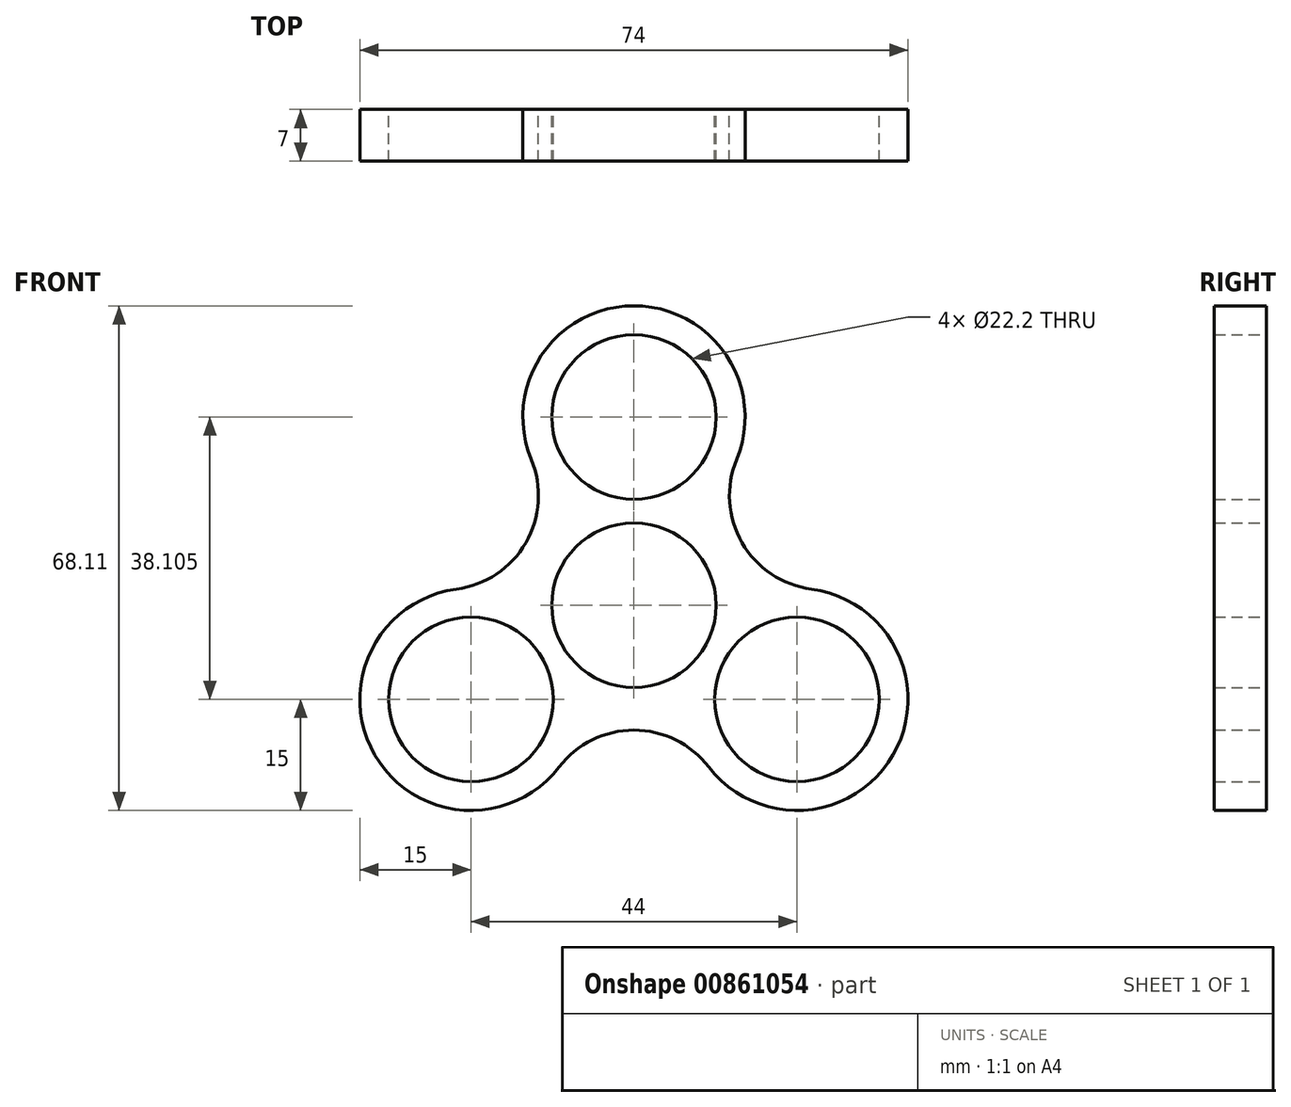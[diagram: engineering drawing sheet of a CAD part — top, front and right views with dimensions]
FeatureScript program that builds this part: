
annotation { "Feature Type Name" : "Feature", "Feature Type Description" : "" }
export const myFeature = defineFeature(function(context is Context, id is Id, definition is map)
    precondition{}
    {
        {
            var Q0;
            Q0=qCreatedBy(makeId("Front.planeOp"),FACE);
            var sketch = newSketch(context, id + "F0", { "sketchPlane" : qUnion([Q0])});
            skLineSegment(sketch, "E0", {"start": v(-22, 0) * mm, "end": v(22, 0) * mm});
            skLineSegment(sketch, "E1", {"start": v(22, 0) * mm, "end": v(0, 38.1) * mm});
            skLineSegment(sketch, "E2", {"start": v(0, 38.1) * mm, "end": v(-22, 0) * mm});
            skCircle(sketch, "E3", {"center": v(22, 0) * mm, "radius": 15 * mm});
            skCircle(sketch, "E4", {"center": v(0, 38.1) * mm, "radius": 15 * mm});
            skCircle(sketch, "E5", {"center": v(-22, 0) * mm, "radius": 15 * mm});
            skLineSegment(sketch, "E6", {"start": v(22, 0) * mm, "end": v(-25.63, 27.5) * mm});
            skLineSegment(sketch, "E7", {"start": v(-22, 0) * mm, "end": v(25.63, 27.5) * mm});
            skLineSegment(sketch, "E8", {"start": v(0, 38.1) * mm, "end": v(0, -16.9) * mm});
            skArc(sketch, "E9", {"start": v(-23.96, 14.87) * mm, "mid": v(-14.6, 21.13) * mm, "end": v(-13.86, 32.37) * mm});
            skArc(sketch, "E10", {"start": v(10.1, -9.14) * mm, "mid": v(0, -4.16) * mm, "end": v(-10.1, -9.14) * mm});
            skArc(sketch, "E11", {"start": v(13.86, 32.37) * mm, "mid": v(14.6, 21.13) * mm, "end": v(23.96, 14.87) * mm});
            skCircle(sketch, "E12", {"center": v(22, 0) * mm, "radius": 11.1 * mm});
            skCircle(sketch, "E13", {"center": v(0, 38.1) * mm, "radius": 11.1 * mm});
            skCircle(sketch, "E14", {"center": v(-22, 0) * mm, "radius": 11.1 * mm});
            skCircle(sketch, "E15", {"center": v(0, 12.7) * mm, "radius": 11.1 * mm});
            skSolve(sketch);
        }
        {
            var Q0;
            Q0 = qSketchRegion(id + "F0", true);
            var Q1;
            {var subQ0=sQuery(id+"F0.wireOp",EDGE,"E3");var subQ1=sQuery(id+"F0.wireOp",EDGE,"E1");var subQ2=makeQuery(id+"F0.imprint","INTERSECT",VERTEX,{"derivedFrom":[subQ1,subQ0]});Q1=makeQuery(id+"F0.imprint","IMPRINT",FACE,{"disambiguationData":[TD([[makeQuery(id+"F0.imprint","IMPRINT",EDGE,{"disambiguationData":[TD([[subQ2,-1.0]])],"derivedFrom":subQ1}),1.0]])]});}
            var Q2;
            {var subQ0=sQuery(id+"F0.wireOp",EDGE,"E12");var subQ1=sQuery(id+"F0.wireOp",EDGE,"E1");var subQ2=makeQuery(id+"F0.imprint","INTERSECT",VERTEX,{"derivedFrom":[subQ1,subQ0]});Q2=makeQuery(id+"F0.imprint","IMPRINT",FACE,{"disambiguationData":[TD([[makeQuery(id+"F0.imprint","IMPRINT",EDGE,{"disambiguationData":[TD([[subQ2,-1.0]])],"derivedFrom":subQ1}),1.0]])]});}
            var Q3;
            {var subQ5=sQuery(id+"F0.wireOp",EDGE,"E3");var subQ7=sQuery(id+"F0.wireOp",EDGE,"E0");var subQ9=makeQuery(id+"F0.imprint","INTERSECT",VERTEX,{"derivedFrom":[subQ7,subQ5]});Q3=makeQuery(id+"F0.imprint","IMPRINT",FACE,{"disambiguationData":[TD([[makeQuery(id+"F0.imprint","IMPRINT",EDGE,{"disambiguationData":[TD([[subQ9,-1.0]])],"derivedFrom":subQ7}),1.0]])]});}
            var Q4;
            {var subQ0=sQuery(id+"F0.wireOp",EDGE,"E7");var subQ1=sQuery(id+"F0.wireOp",EDGE,"E1");var subQ2=makeQuery(id+"F0.imprint","INTERSECT",VERTEX,{"derivedFrom":[subQ1,subQ0]});Q4=makeQuery(id+"F0.imprint","IMPRINT",FACE,{"disambiguationData":[TD([[makeQuery(id+"F0.imprint","IMPRINT",EDGE,{"disambiguationData":[TD([[subQ2,-1.0]])],"derivedFrom":subQ1}),1.0]])]});}
            var Q5;
            {var subQ5=sQuery(id+"F0.wireOp",EDGE,"E4");var subQ6=sQuery(id+"F0.wireOp",EDGE,"E1");var subQ7=makeQuery(id+"F0.imprint","INTERSECT",VERTEX,{"derivedFrom":[subQ6,subQ5]});Q5=makeQuery(id+"F0.imprint","IMPRINT",FACE,{"disambiguationData":[TD([[makeQuery(id+"F0.imprint","IMPRINT",EDGE,{"disambiguationData":[TD([[subQ7,-1.0]])],"derivedFrom":subQ6}),1.0]])]});}
            var Q6;
            {var subQ0=sQuery(id+"F0.wireOp",EDGE,"E13");var subQ1=sQuery(id+"F0.wireOp",EDGE,"E2");var subQ2=makeQuery(id+"F0.imprint","INTERSECT",VERTEX,{"derivedFrom":[subQ1,subQ0]});Q6=makeQuery(id+"F0.imprint","IMPRINT",FACE,{"disambiguationData":[TD([[makeQuery(id+"F0.imprint","IMPRINT",EDGE,{"disambiguationData":[TD([[subQ2,-1.0]])],"derivedFrom":subQ1}),1.0]])]});}
            var Q7;
            {var subQ0=sQuery(id+"F0.wireOp",EDGE,"E4");var subQ1=sQuery(id+"F0.wireOp",EDGE,"E2");var subQ2=makeQuery(id+"F0.imprint","INTERSECT",VERTEX,{"derivedFrom":[subQ1,subQ0]});Q7=makeQuery(id+"F0.imprint","IMPRINT",FACE,{"disambiguationData":[TD([[makeQuery(id+"F0.imprint","IMPRINT",EDGE,{"disambiguationData":[TD([[subQ2,-1.0]])],"derivedFrom":subQ1}),1.0]])]});}
            var Q8;
            {var subQ0=sQuery(id+"F0.wireOp",EDGE,"E6");var subQ1=sQuery(id+"F0.wireOp",EDGE,"E2");var subQ2=makeQuery(id+"F0.imprint","INTERSECT",VERTEX,{"derivedFrom":[subQ1,subQ0]});Q8=makeQuery(id+"F0.imprint","IMPRINT",FACE,{"disambiguationData":[TD([[makeQuery(id+"F0.imprint","IMPRINT",EDGE,{"disambiguationData":[TD([[subQ2,-1.0]])],"derivedFrom":subQ1}),1.0]])]});}
            var Q9;
            {var subQ1=sQuery(id+"F0.wireOp",EDGE,"E2");var subQ7=sQuery(id+"F0.wireOp",EDGE,"E5");var subQ9=makeQuery(id+"F0.imprint","INTERSECT",VERTEX,{"derivedFrom":[subQ1,subQ7]});Q9=makeQuery(id+"F0.imprint","IMPRINT",FACE,{"disambiguationData":[TD([[makeQuery(id+"F0.imprint","IMPRINT",EDGE,{"disambiguationData":[TD([[subQ9,-1.0]])],"derivedFrom":subQ1}),1.0]])]});}
            var Q10;
            {var subQ0=sQuery(id+"F0.wireOp",EDGE,"E14");var subQ1=sQuery(id+"F0.wireOp",EDGE,"E0");var subQ2=makeQuery(id+"F0.imprint","INTERSECT",VERTEX,{"derivedFrom":[subQ1,subQ0]});Q10=makeQuery(id+"F0.imprint","IMPRINT",FACE,{"disambiguationData":[TD([[makeQuery(id+"F0.imprint","IMPRINT",EDGE,{"disambiguationData":[TD([[subQ2,-1.0]])],"derivedFrom":subQ1}),1.0]])]});}
            var Q11;
            {var subQ0=sQuery(id+"F0.wireOp",EDGE,"E8");var subQ1=sQuery(id+"F0.wireOp",EDGE,"E0");var subQ2=makeQuery(id+"F0.imprint","INTERSECT",VERTEX,{"derivedFrom":[subQ1,subQ0]});Q11=makeQuery(id+"F0.imprint","IMPRINT",FACE,{"disambiguationData":[TD([[makeQuery(id+"F0.imprint","IMPRINT",EDGE,{"disambiguationData":[TD([[subQ2,-1.0]])],"derivedFrom":subQ1}),1.0]])]});}
            var Q12;
            {var subQ0=sQuery(id+"F0.wireOp",EDGE,"E5");var subQ1=sQuery(id+"F0.wireOp",EDGE,"E0");var subQ2=makeQuery(id+"F0.imprint","INTERSECT",VERTEX,{"derivedFrom":[subQ1,subQ0]});Q12=makeQuery(id+"F0.imprint","IMPRINT",FACE,{"disambiguationData":[TD([[makeQuery(id+"F0.imprint","IMPRINT",EDGE,{"disambiguationData":[TD([[subQ2,-1.0]])],"derivedFrom":subQ1}),1.0]])]});}
            extrude(context, id + "F1", {"entities" : qUnion([Q0, Q1, Q2, Q3, Q4, Q5, Q6, Q7, Q8, Q9, Q10, Q11, Q12]), "depth" : 7 * mm, "offsetDistance" : 25 * mm});
        }
    });
